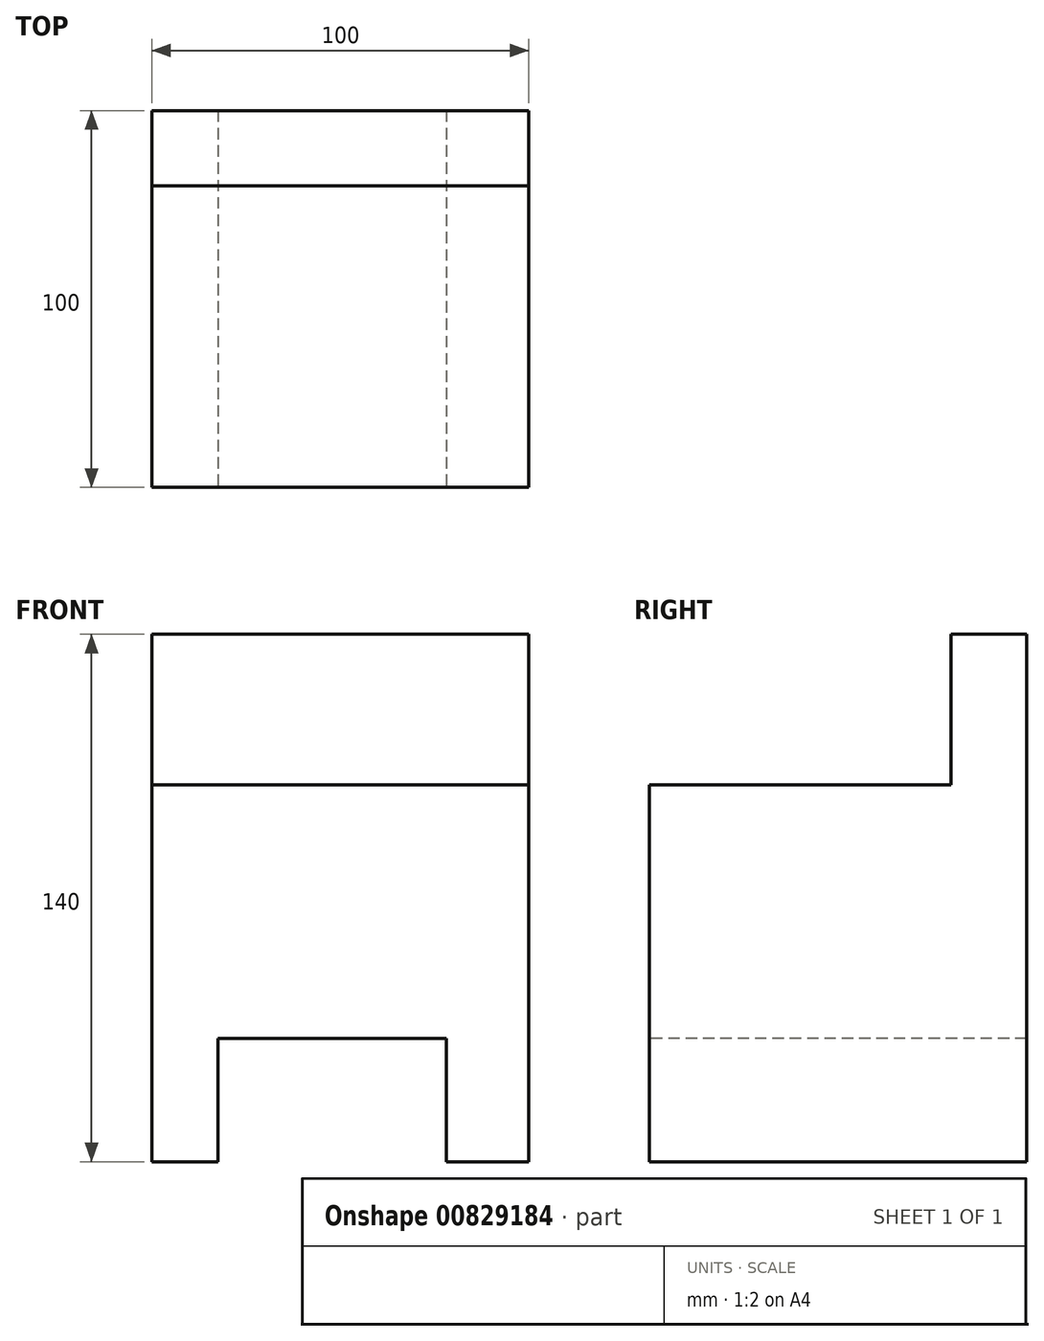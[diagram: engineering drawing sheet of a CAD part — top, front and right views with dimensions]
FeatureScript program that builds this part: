
annotation { "Feature Type Name" : "Feature", "Feature Type Description" : "" }
export const myFeature = defineFeature(function(context is Context, id is Id, definition is map)
    precondition{}
    {
        {
            var Q0;
            Q0=qCreatedBy(makeId("Top.planeOp"),FACE);
            var sketch = newSketch(context, id + "F0", { "sketchPlane" : qUnion([Q0])});
            skLineSegment(sketch, "E0.bottom", {"start": v(-50, -50) * mm, "end": v(50, -50) * mm});
            skLineSegment(sketch, "E0.top", {"start": v(-50, 50) * mm, "end": v(50, 50) * mm});
            skLineSegment(sketch, "E0.left", {"start": v(-50, -50) * mm, "end": v(-50, 50) * mm});
            skLineSegment(sketch, "E0.right", {"start": v(50, -50) * mm, "end": v(50, 50) * mm});
            skPoint(sketch, "E0.middle", {"position": v(0, 0) * mm});
            skSolve(sketch);
        }
        {
            var Q0;
            Q0 = qSketchRegion(id + "F0", true);
            extrude(context, id + "F1", {"entities" : qUnion([Q0]), "depth" : 100 * mm, "offsetDistance" : 25 * mm});
        }
        {
            var Q0;
            Q0=makeQuery(id+"F1.opExtrude","CAP_FACE",FACE,{"disambiguationData":[OSD([sQuery(id+"F0.wireOp",EDGE,"E0.bottom"),sQuery(id+"F0.wireOp",EDGE,"E0.top"),sQuery(id+"F0.wireOp",EDGE,"E0.left"),sQuery(id+"F0.wireOp",EDGE,"E0.right")])],"isStart":false});
            var sketch = newSketch(context, id + "F2", { "sketchPlane" : qUnion([Q0])});
            skLineSegment(sketch, "E1.bottom", {"start": v(-50, -50) * mm, "end": v(50, -50) * mm});
            skLineSegment(sketch, "E1.top", {"start": v(-50, 30) * mm, "end": v(50, 30) * mm});
            skLineSegment(sketch, "E1.left", {"start": v(-50, -50) * mm, "end": v(-50, 30) * mm});
            skLineSegment(sketch, "E1.right", {"start": v(50, -50) * mm, "end": v(50, 30) * mm});
            skSolve(sketch);
        }
        {
            var Q0;
            {var subQ0=sQuery(id+"F2.wireOp",EDGE,"E1.top");Q0=makeQuery(id+"F2.imprint","IMPRINT",FACE,{"disambiguationData":[TD([[makeQuery(id+"F2.imprint","IMPRINT",EDGE,{"derivedFrom":subQ0}),1.0]])]});}
            extrude(context, id + "F3", {"entities" : qUnion([Q0]), "operationType" : NewBodyOperationType.ADD, "depth" : 40 * mm, "offsetDistance" : 25 * mm});
        }
        {
            var Q0;
            Q0=makeQuery(id+"F1.opExtrude","SWEPT_FACE",FACE,{"disambiguationData":[OSD([sQuery(id+"F0.wireOp",EDGE,"E0.bottom")])]});
            var sketch = newSketch(context, id + "F4", { "sketchPlane" : qUnion([Q0])});
            skLineSegment(sketch, "E2.bottom", {"start": v(-32.44, 32.75) * mm, "end": v(28.12, 32.75) * mm});
            skLineSegment(sketch, "E2.top", {"start": v(-32.44, 0) * mm, "end": v(28.12, 0) * mm});
            skLineSegment(sketch, "E2.left", {"start": v(-32.44, 32.75) * mm, "end": v(-32.44, 0) * mm});
            skLineSegment(sketch, "E2.right", {"start": v(28.12, 32.75) * mm, "end": v(28.12, 0) * mm});
            skSolve(sketch);
        }
        {
            var Q0;
            Q0 = qSketchRegion(id + "F4", true);
            extrude(context, id + "F5", {"entities" : qUnion([Q0]), "operationType" : NewBodyOperationType.REMOVE, "endBound" : BoundingType.THROUGH_ALL, "oppositeDirection" : true, "depth" : 25 * mm, "offsetDistance" : 25 * mm});
        }
    });
